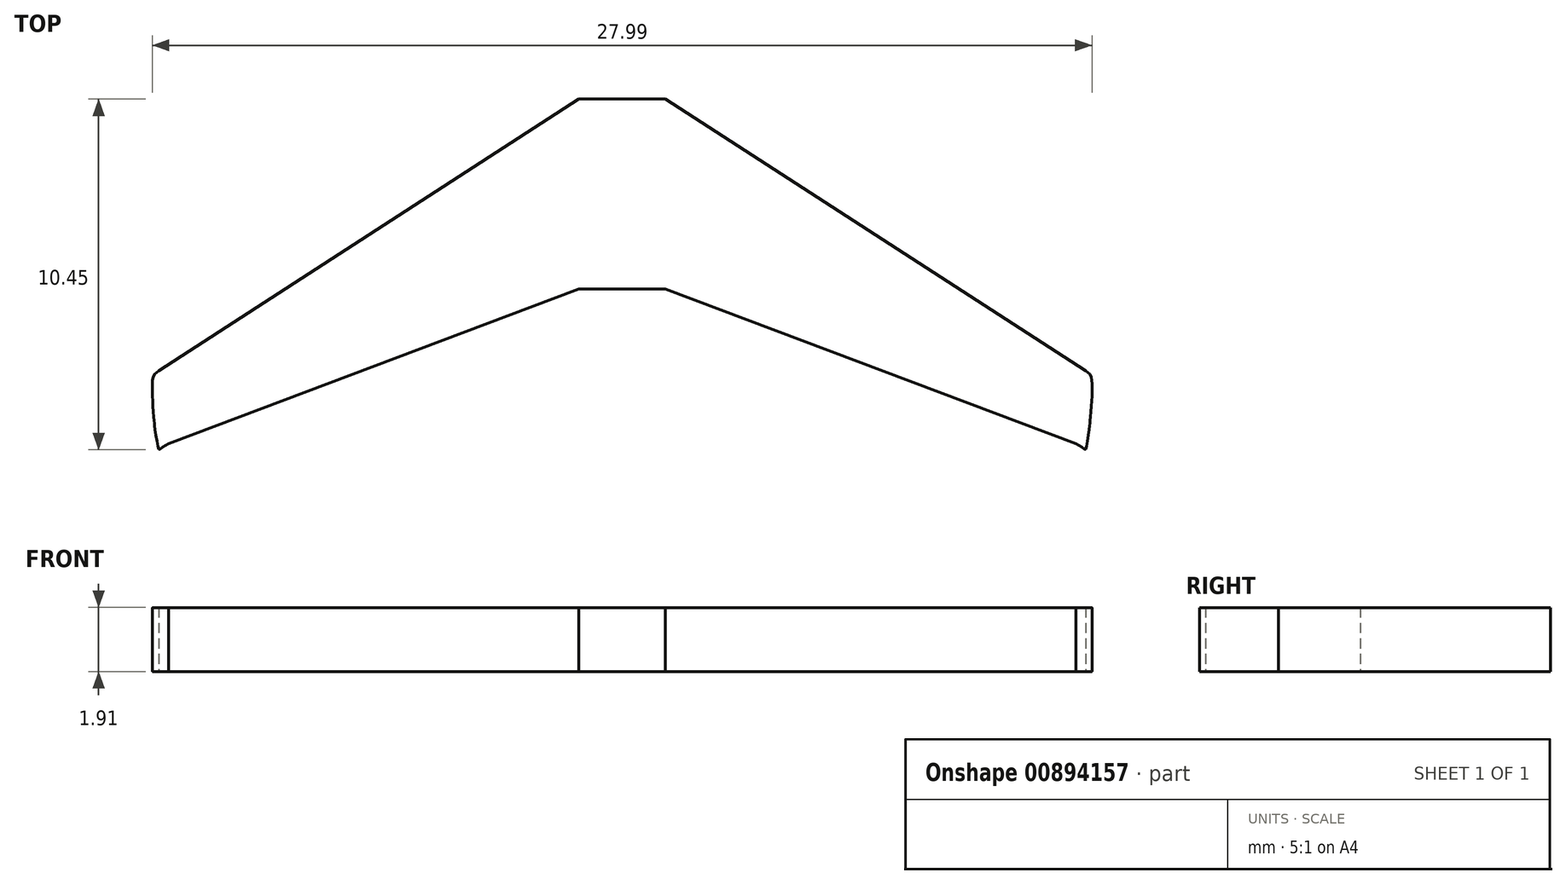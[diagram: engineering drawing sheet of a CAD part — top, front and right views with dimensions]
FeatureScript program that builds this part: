
annotation { "Feature Type Name" : "Feature", "Feature Type Description" : "" }
export const myFeature = defineFeature(function(context is Context, id is Id, definition is map)
    precondition{}
    {
        {
            var Q0;
            Q0=qCreatedBy(makeId("Top.planeOp"),FACE);
            var sketch = newSketch(context, id + "F0", { "sketchPlane" : qUnion([Q0])});
            skLineSegment(sketch, "E0.MirrorCS", {"start": v(1.55, -2.53) * mm, "end": v(14.06, -10.63) * mm});
            skLineSegment(sketch, "E1.MirrorCS", {"start": v(13.77, -12.8) * mm, "end": v(1.54, -8.19) * mm});
            skLineSegment(sketch, "E2", {"start": v(1.54, -2.53) * mm, "end": v(1.54, -8.19) * mm});
            skLineSegment(sketch, "E3.bottom", {"start": v(1.55, -2.53) * mm, "end": v(0.26, -2.53) * mm});
            skLineSegment(sketch, "E3.top", {"start": v(1.55, -8.19) * mm, "end": v(0.26, -8.19) * mm});
            skLineSegment(sketch, "E3.left", {"start": v(1.55, -2.53) * mm, "end": v(1.55, -8.19) * mm});
            skLineSegment(sketch, "E3.right", {"start": v(0.26, -2.53) * mm, "end": v(0.26, -8.19) * mm});
            skLineSegment(sketch, "E4.MirrorCS", {"start": v(-1.04, -2.53) * mm, "end": v(0.26, -2.53) * mm});
            skLineSegment(sketch, "E5.MirrorCS", {"start": v(-1.03, -2.53) * mm, "end": v(-1.03, -8.19) * mm});
            skLineSegment(sketch, "E6.MirrorCS", {"start": v(-13.26, -12.8) * mm, "end": v(-1.03, -8.19) * mm});
            skLineSegment(sketch, "E7.MirrorCS", {"start": v(-1.04, -8.19) * mm, "end": v(0.26, -8.19) * mm});
            skLineSegment(sketch, "E8.MirrorCS", {"start": v(-1.04, -2.53) * mm, "end": v(-13.55, -10.63) * mm});
            skFitSpline(sketch, "E9", {"points": [v(14.06, -10.63) * mm, v(14.2, -10.77) * mm, v(14.25, -11.06) * mm, v(14.24, -11.55) * mm, v(14.2, -12.15) * mm, v(14.18, -12.3) * mm, v(14.06, -12.96) * mm, v(13.77, -12.8) * mm], "startDerivative": vector(1.55, -1.08) * mm, "endDerivative": vector(-5.64, 2.52) * mm});
            skFitSpline(sketch, "E10.MirrorCS", {"points": [v(-13.55, -10.63) * mm, v(-13.7, -10.77) * mm, v(-13.74, -11.06) * mm, v(-13.73, -11.55) * mm, v(-13.68, -12.15) * mm, v(-13.67, -12.3) * mm, v(-13.55, -12.96) * mm, v(-13.26, -12.8) * mm], "startDerivative": vector(-1.55, -1.08) * mm, "endDerivative": vector(5.64, 2.52) * mm});
            skSolve(sketch);
        }
        {
            var Q0;
            Q0 = qSketchRegion(id + "F0", true);
            extrude(context, id + "F1", {"entities" : qUnion([Q0]), "depth" : 1.9 * mm, "offsetDistance" : 25.4 * mm});
        }
    });
